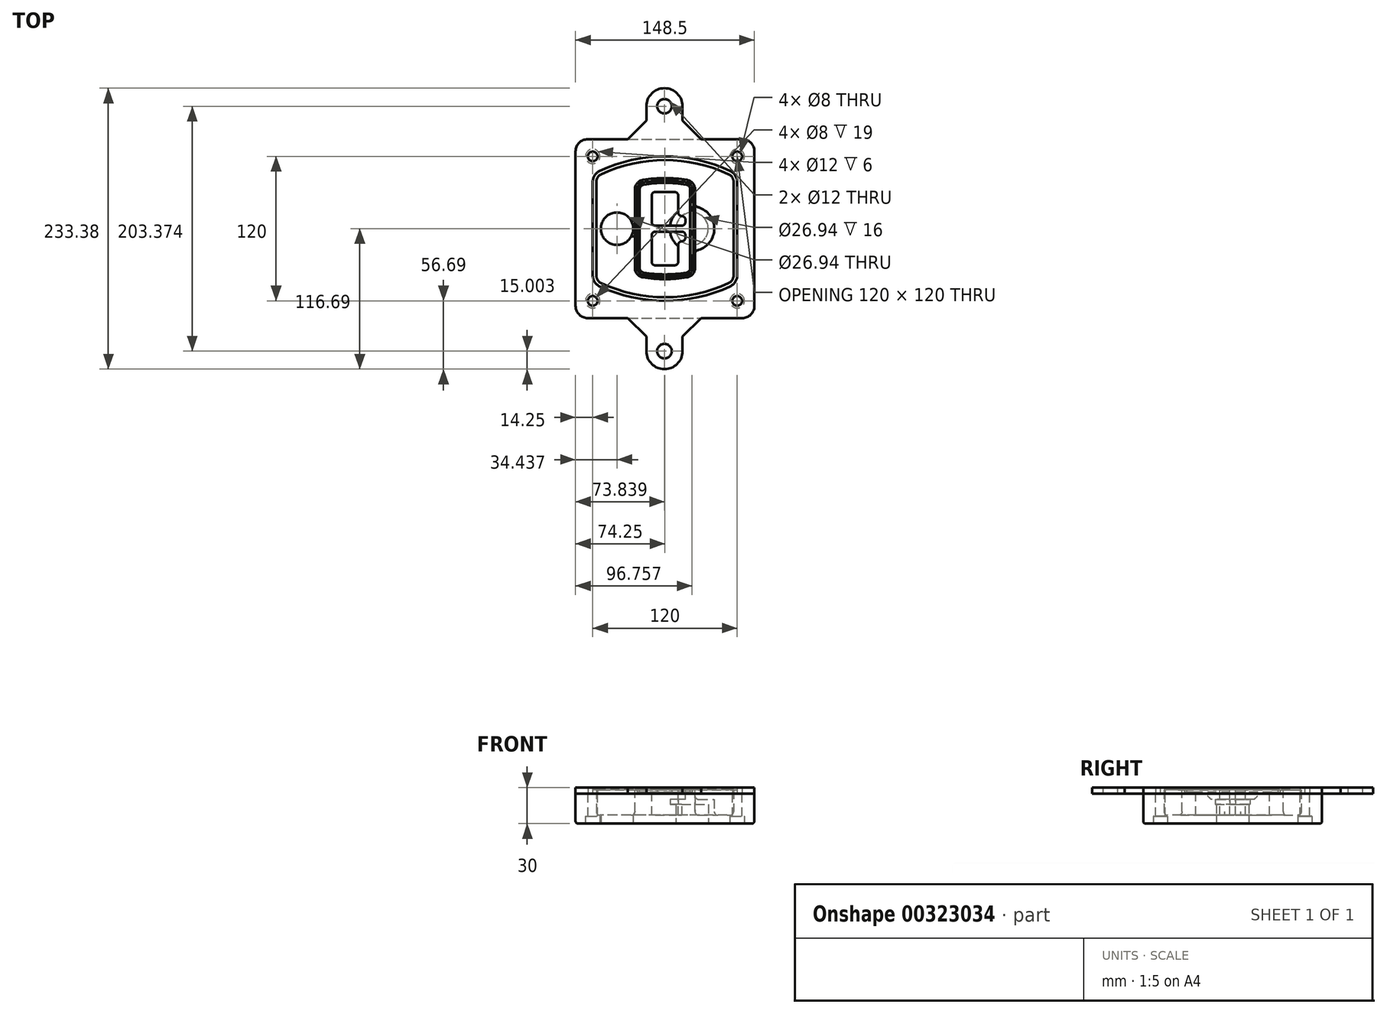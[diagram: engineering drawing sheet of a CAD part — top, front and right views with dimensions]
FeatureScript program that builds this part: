
annotation { "Feature Type Name" : "Feature", "Feature Type Description" : "" }
export const myFeature = defineFeature(function(context is Context, id is Id, definition is map)
    precondition{}
    {
        {
            var Q0;
            Q0=qCreatedBy(makeId("Top.planeOp"),FACE);
            var sketch = newSketch(context, id + "F0", { "sketchPlane" : qUnion([Q0])});
            skPoint(sketch, "E0.rect.middle", {"position": v(0, 0) * mm});
            skLineSegment(sketch, "E1.bottom", {"start": v(-64.25, -74.25) * mm, "end": v(64.25, -74.25) * mm});
            skLineSegment(sketch, "E1.top", {"start": v(-64.25, 74.25) * mm, "end": v(64.25, 74.25) * mm});
            skLineSegment(sketch, "E1.left", {"start": v(-74.25, -64.25) * mm, "end": v(-74.25, 64.25) * mm});
            skLineSegment(sketch, "E1.right", {"start": v(74.25, -64.25) * mm, "end": v(74.25, 64.25) * mm});
            skLineSegment(sketch, "E2", {"start": v(-74.25, 74.25) * mm, "end": v(74.25, -74.25) * mm, "construction": true});
            skLineSegment(sketch, "E3", {"start": v(74.25, 74.25) * mm, "end": v(-74.25, -74.25) * mm, "construction": true});
            skCircle(sketch, "E4", {"center": v(-60, 60) * mm, "radius": 4 * mm});
            skCircle(sketch, "E5", {"center": v(60, 60) * mm, "radius": 4 * mm});
            skCircle(sketch, "E6", {"center": v(60, -60) * mm, "radius": 4 * mm});
            skCircle(sketch, "E7", {"center": v(-60, -60) * mm, "radius": 4 * mm});
            skLineSegment(sketch, "E8", {"start": v(-60, 60) * mm, "end": v(60, 60) * mm, "construction": true});
            skLineSegment(sketch, "E9", {"start": v(60, 60) * mm, "end": v(60, -60) * mm, "construction": true});
            skLineSegment(sketch, "E10", {"start": v(60, -60) * mm, "end": v(-60, -60) * mm, "construction": true});
            skLineSegment(sketch, "E11", {"start": v(-60, -60) * mm, "end": v(-60, 60) * mm, "construction": true});
            skLineSegment(sketch, "E12", {"start": v(-60, 38.83) * mm, "end": v(-60, -38.83) * mm});
            skLineSegment(sketch, "E13", {"start": v(60, 38.83) * mm, "end": v(60, -38.83) * mm});
            skArc(sketch, "E14", {"start": v(54.26, 47.88) * mm, "mid": v(0, 60) * mm, "end": v(-54.26, 47.88) * mm});
            skArc(sketch, "E15", {"start": v(-54.26, -47.88) * mm, "mid": v(0, -60) * mm, "end": v(54.26, -47.88) * mm});
            skLineSegment(sketch, "E16", {"start": v(-60, 0) * mm, "end": v(60, 0) * mm, "construction": true});
            skPoint(sketch, "E17.visualSharp", {"position": v(-60, -45) * mm});
            skArc(sketch, "E17.filletArc", {"start": v(-60, -38.83) * mm, "mid": v(-58.44, -44.2) * mm, "end": v(-54.26, -47.88) * mm});
            skPoint(sketch, "E18.visualSharp", {"position": v(-60, 45) * mm});
            skArc(sketch, "E18.filletArc", {"start": v(-54.26, 47.88) * mm, "mid": v(-58.44, 44.2) * mm, "end": v(-60, 38.83) * mm});
            skPoint(sketch, "E19.visualSharp", {"position": v(60, 45) * mm});
            skArc(sketch, "E19.filletArc", {"start": v(60, 38.83) * mm, "mid": v(58.44, 44.2) * mm, "end": v(54.26, 47.88) * mm});
            skPoint(sketch, "E20.visualSharp", {"position": v(60, -45) * mm});
            skArc(sketch, "E20.filletArc", {"start": v(54.26, -47.88) * mm, "mid": v(58.44, -44.2) * mm, "end": v(60, -38.83) * mm});
            skPoint(sketch, "E21.visualSharp", {"position": v(-74.25, 74.25) * mm});
            skArc(sketch, "E21.filletArc", {"start": v(-64.25, 74.25) * mm, "mid": v(-71.32, 71.32) * mm, "end": v(-74.25, 64.25) * mm});
            skPoint(sketch, "E22.visualSharp", {"position": v(74.25, 74.25) * mm});
            skArc(sketch, "E22.filletArc", {"start": v(74.25, 64.25) * mm, "mid": v(71.32, 71.32) * mm, "end": v(64.25, 74.25) * mm});
            skPoint(sketch, "E23.visualSharp", {"position": v(74.25, -74.25) * mm});
            skArc(sketch, "E23.filletArc", {"start": v(64.25, -74.25) * mm, "mid": v(71.32, -71.32) * mm, "end": v(74.25, -64.25) * mm});
            skPoint(sketch, "E24.visualSharp", {"position": v(-74.25, -74.25) * mm});
            skArc(sketch, "E24.filletArc", {"start": v(-74.25, -64.25) * mm, "mid": v(-71.32, -71.32) * mm, "end": v(-64.25, -74.25) * mm});
            skArc(sketch, "E25.0", {"start": v(57, 38.83) * mm, "mid": v(55.9, 42.58) * mm, "end": v(52.98, 45.17) * mm});
            skLineSegment(sketch, "E25.1", {"start": v(57, 38.83) * mm, "end": v(57, -38.83) * mm});
            skArc(sketch, "E25.2", {"start": v(52.98, -45.17) * mm, "mid": v(55.9, -42.58) * mm, "end": v(57, -38.83) * mm});
            skArc(sketch, "E25.3", {"start": v(-52.98, -45.17) * mm, "mid": v(0, -57) * mm, "end": v(52.98, -45.17) * mm});
            skArc(sketch, "E25.4", {"start": v(-57, -38.83) * mm, "mid": v(-55.9, -42.58) * mm, "end": v(-52.98, -45.17) * mm});
            skArc(sketch, "E25.5", {"start": v(52.98, 45.17) * mm, "mid": v(0, 57) * mm, "end": v(-52.98, 45.17) * mm});
            skLineSegment(sketch, "E25.6", {"start": v(-57, 38.83) * mm, "end": v(-57, -38.83) * mm});
            skArc(sketch, "E25.7", {"start": v(-52.98, 45.17) * mm, "mid": v(-55.9, 42.58) * mm, "end": v(-57, 38.83) * mm});
            skArc(sketch, "E26.0", {"start": v(-55.96, 51.5) * mm, "mid": v(-61.82, 46.33) * mm, "end": v(-64, 38.83) * mm});
            skArc(sketch, "E26.1", {"start": v(55.96, 51.5) * mm, "mid": v(0, 64) * mm, "end": v(-55.96, 51.5) * mm});
            skArc(sketch, "E26.2", {"start": v(64, 38.83) * mm, "mid": v(61.82, 46.33) * mm, "end": v(55.96, 51.5) * mm});
            skLineSegment(sketch, "E26.3", {"start": v(64, 38.83) * mm, "end": v(64, -38.83) * mm});
            skArc(sketch, "E26.4", {"start": v(55.96, -51.5) * mm, "mid": v(61.82, -46.33) * mm, "end": v(64, -38.83) * mm});
            skLineSegment(sketch, "E26.5", {"start": v(-64, 38.83) * mm, "end": v(-64, -38.83) * mm});
            skArc(sketch, "E26.6", {"start": v(-55.96, -51.5) * mm, "mid": v(0, -64) * mm, "end": v(55.96, -51.5) * mm});
            skArc(sketch, "E26.7", {"start": v(-64, -38.83) * mm, "mid": v(-61.82, -46.33) * mm, "end": v(-55.96, -51.5) * mm});
            skSolve(sketch);
        }
        {
            var Q0;
            Q0=makeQuery(id+"F0.imprint","IMPRINT",FACE,{"disambiguationData":[TD([[makeQuery(id+"F0.imprint","IMPRINT",EDGE,{"derivedFrom":sQuery(id+"F0.wireOp",EDGE,"E1.bottom")}),1.0]])]});
            var Q1;
            Q1=makeQuery(id+"F0.imprint","IMPRINT",FACE,{"disambiguationData":[TD([[makeQuery(id+"F0.imprint","IMPRINT",EDGE,{"derivedFrom":sQuery(id+"F0.wireOp",EDGE,"E12")}),1.0]])]});
            var Q2;
            Q2=makeQuery(id+"F0.imprint","IMPRINT",FACE,{"disambiguationData":[TD([[makeQuery(id+"F0.imprint","IMPRINT",EDGE,{"derivedFrom":sQuery(id+"F0.wireOp",EDGE,"E25.0")}),1.0]])]});
            var Q3;
            Q3=makeQuery(id+"F0.imprint","IMPRINT",FACE,{"disambiguationData":[TD([[makeQuery(id+"F0.imprint","IMPRINT",EDGE,{"derivedFrom":sQuery(id+"F0.wireOp",EDGE,"E12")}),-1.0]])]});
            extrude(context, id + "F1", {"entities" : qUnion([Q0, Q1, Q2, Q3]), "oppositeDirection" : true, "depth" : 25 * mm});
        }
        {
            var Q0;
            Q0=makeQuery(id+"F0.imprint","IMPRINT",FACE,{"disambiguationData":[TD([[makeQuery(id+"F0.imprint","IMPRINT",EDGE,{"derivedFrom":sQuery(id+"F0.wireOp",EDGE,"E12")}),1.0]])]});
            extrude(context, id + "F2", {"entities" : qUnion([Q0]), "operationType" : NewBodyOperationType.ADD, "depth" : 3 * mm});
        }
        {
            var Q0;
            Q0=makeQuery(id+"F0.imprint","IMPRINT",FACE,{"disambiguationData":[TD([[makeQuery(id+"F0.imprint","IMPRINT",EDGE,{"derivedFrom":sQuery(id+"F0.wireOp",EDGE,"E25.0")}),1.0]])]});
            extrude(context, id + "F3", {"entities" : qUnion([Q0]), "operationType" : NewBodyOperationType.REMOVE, "oppositeDirection" : true, "depth" : 18 * mm});
        }
        {
            var Q0;
            Q0=makeQuery(id+"F2.opExtrude","CAP_FACE",FACE,{"disambiguationData":[OSD([sQuery(id+"F0.wireOp",EDGE,"E12"),sQuery(id+"F0.wireOp",EDGE,"E13"),sQuery(id+"F0.wireOp",EDGE,"E14"),sQuery(id+"F0.wireOp",EDGE,"E15"),sQuery(id+"F0.wireOp",EDGE,"E17.filletArc"),sQuery(id+"F0.wireOp",EDGE,"E18.filletArc"),sQuery(id+"F0.wireOp",EDGE,"E19.filletArc"),sQuery(id+"F0.wireOp",EDGE,"E20.filletArc"),sQuery(id+"F0.wireOp",EDGE,"E25.0"),sQuery(id+"F0.wireOp",EDGE,"E25.1"),sQuery(id+"F0.wireOp",EDGE,"E25.2"),sQuery(id+"F0.wireOp",EDGE,"E25.3"),sQuery(id+"F0.wireOp",EDGE,"E25.4"),sQuery(id+"F0.wireOp",EDGE,"E25.5"),sQuery(id+"F0.wireOp",EDGE,"E25.6"),sQuery(id+"F0.wireOp",EDGE,"E25.7")])],"isStart":false});
            var sketch = newSketch(context, id + "F4", { "sketchPlane" : qUnion([Q0])});
            skArc(sketch, "E27.0", {"start": v(-18.34, -40.45) * mm, "mid": v(0, -42) * mm, "end": v(18.34, -40.45) * mm});
            skArc(sketch, "E28.0", {"start": v(18.34, 40.45) * mm, "mid": v(0, 42) * mm, "end": v(-18.34, 40.45) * mm});
            skLineSegment(sketch, "E29", {"start": v(-25, 32.57) * mm, "end": v(-25, -32.57) * mm});
            skLineSegment(sketch, "E30", {"start": v(25, 32.57) * mm, "end": v(25, -32.57) * mm});
            skLineSegment(sketch, "E31", {"start": v(-25, 39.1) * mm, "end": v(25, 39.1) * mm, "construction": true});
            skLineSegment(sketch, "E32", {"start": v(-25, -39.1) * mm, "end": v(25, -39.1) * mm, "construction": true});
            skPoint(sketch, "E33.visualSharp", {"position": v(-25, 39.1) * mm});
            skArc(sketch, "E33.filletArc", {"start": v(-18.34, 40.45) * mm, "mid": v(-23.11, 37.73) * mm, "end": v(-25, 32.57) * mm});
            skPoint(sketch, "E34.visualSharp", {"position": v(25, 39.1) * mm});
            skArc(sketch, "E34.filletArc", {"start": v(25, 32.57) * mm, "mid": v(23.11, 37.73) * mm, "end": v(18.34, 40.45) * mm});
            skPoint(sketch, "E35.visualSharp", {"position": v(25, -39.1) * mm});
            skArc(sketch, "E35.filletArc", {"start": v(18.34, -40.45) * mm, "mid": v(23.11, -37.73) * mm, "end": v(25, -32.57) * mm});
            skPoint(sketch, "E36.visualSharp", {"position": v(-25, -39.1) * mm});
            skArc(sketch, "E36.filletArc", {"start": v(-25, -32.57) * mm, "mid": v(-23.11, -37.73) * mm, "end": v(-18.34, -40.45) * mm});
            skArc(sketch, "E37.0", {"start": v(52.98, 45.17) * mm, "mid": v(0, 57) * mm, "end": v(-52.98, 45.17) * mm});
            skArc(sketch, "E37.1", {"start": v(-52.98, 45.17) * mm, "mid": v(-55.9, 42.58) * mm, "end": v(-57, 38.83) * mm});
            skLineSegment(sketch, "E37.2", {"start": v(-57, 38.83) * mm, "end": v(-57, -38.83) * mm});
            skArc(sketch, "E37.3", {"start": v(-57, -38.83) * mm, "mid": v(-55.9, -42.58) * mm, "end": v(-52.98, -45.17) * mm});
            skArc(sketch, "E37.4", {"start": v(-52.98, -45.17) * mm, "mid": v(0, -57) * mm, "end": v(52.98, -45.17) * mm});
            skArc(sketch, "E37.5", {"start": v(52.98, -45.17) * mm, "mid": v(55.9, -42.58) * mm, "end": v(57, -38.83) * mm});
            skLineSegment(sketch, "E37.6", {"start": v(57, 38.83) * mm, "end": v(57, -38.83) * mm});
            skArc(sketch, "E37.7", {"start": v(57, 38.83) * mm, "mid": v(55.9, 42.58) * mm, "end": v(52.98, 45.17) * mm});
            skLineSegment(sketch, "E38.0", {"start": v(23, 32.57) * mm, "end": v(23, -32.57) * mm});
            skArc(sketch, "E38.1", {"start": v(18, -38.48) * mm, "mid": v(21.58, -36.44) * mm, "end": v(23, -32.57) * mm});
            skArc(sketch, "E38.2", {"start": v(-18, -38.48) * mm, "mid": v(0, -40) * mm, "end": v(18, -38.48) * mm});
            skArc(sketch, "E38.3", {"start": v(-23, -32.57) * mm, "mid": v(-21.58, -36.44) * mm, "end": v(-18, -38.48) * mm});
            skLineSegment(sketch, "E38.4", {"start": v(-23, 32.57) * mm, "end": v(-23, -32.57) * mm});
            skArc(sketch, "E38.5", {"start": v(23, 32.57) * mm, "mid": v(21.58, 36.44) * mm, "end": v(18, 38.48) * mm});
            skArc(sketch, "E38.6", {"start": v(-18, 38.48) * mm, "mid": v(-21.58, 36.44) * mm, "end": v(-23, 32.57) * mm});
            skArc(sketch, "E38.7", {"start": v(18, 38.48) * mm, "mid": v(0, 40) * mm, "end": v(-18, 38.48) * mm});
            skArc(sketch, "E39.0", {"start": v(21, 32.57) * mm, "mid": v(20.06, 35.15) * mm, "end": v(17.67, 36.5) * mm});
            skLineSegment(sketch, "E39.1", {"start": v(21, 32.57) * mm, "end": v(21, -32.57) * mm});
            skArc(sketch, "E39.2", {"start": v(17.67, -36.5) * mm, "mid": v(20.06, -35.15) * mm, "end": v(21, -32.57) * mm});
            skArc(sketch, "E39.3", {"start": v(-17.67, -36.5) * mm, "mid": v(0, -38) * mm, "end": v(17.67, -36.5) * mm});
            skArc(sketch, "E39.4", {"start": v(-21, -32.57) * mm, "mid": v(-20.06, -35.15) * mm, "end": v(-17.67, -36.5) * mm});
            skArc(sketch, "E39.5", {"start": v(17.67, 36.5) * mm, "mid": v(0, 38) * mm, "end": v(-17.67, 36.5) * mm});
            skLineSegment(sketch, "E39.6", {"start": v(-21, 32.57) * mm, "end": v(-21, -32.57) * mm});
            skArc(sketch, "E39.7", {"start": v(-17.67, 36.5) * mm, "mid": v(-20.06, 35.15) * mm, "end": v(-21, 32.57) * mm});
            skLineSegment(sketch, "E40", {"start": v(-25, 0) * mm, "end": v(25, 0) * mm, "construction": true});
            skLineSegment(sketch, "E41", {"start": v(-11, 5.5) * mm, "end": v(-11, 27.5) * mm});
            skLineSegment(sketch, "E42", {"start": v(-8, 30.5) * mm, "end": v(8, 30.5) * mm});
            skLineSegment(sketch, "E43", {"start": v(11, 27.5) * mm, "end": v(11, 13.5) * mm});
            skLineSegment(sketch, "E44", {"start": v(14, 10.5) * mm, "end": v(14, 10.5) * mm});
            skLineSegment(sketch, "E45", {"start": v(17, 7.5) * mm, "end": v(17, 5.5) * mm});
            skLineSegment(sketch, "E46", {"start": v(14, 2.5) * mm, "end": v(-8, 2.5) * mm});
            skPoint(sketch, "E47.visualSharp", {"position": v(-11, 30.5) * mm});
            skArc(sketch, "E47.filletArc", {"start": v(-8, 30.5) * mm, "mid": v(-10.12, 29.62) * mm, "end": v(-11, 27.5) * mm});
            skPoint(sketch, "E48.visualSharp", {"position": v(11, 30.5) * mm});
            skArc(sketch, "E48.filletArc", {"start": v(11, 27.5) * mm, "mid": v(10.12, 29.62) * mm, "end": v(8, 30.5) * mm});
            skPoint(sketch, "E49.visualSharp", {"position": v(11, 10.5) * mm});
            skArc(sketch, "E49.filletArc", {"start": v(11, 13.5) * mm, "mid": v(11.88, 11.38) * mm, "end": v(14, 10.5) * mm});
            skPoint(sketch, "E50.visualSharp", {"position": v(17, 10.5) * mm});
            skArc(sketch, "E50.filletArc", {"start": v(17, 7.5) * mm, "mid": v(16.12, 9.62) * mm, "end": v(14, 10.5) * mm});
            skPoint(sketch, "E51.visualSharp", {"position": v(17, 2.5) * mm});
            skArc(sketch, "E51.filletArc", {"start": v(14, 2.5) * mm, "mid": v(16.12, 3.38) * mm, "end": v(17, 5.5) * mm});
            skPoint(sketch, "E52.visualSharp", {"position": v(-11, 2.5) * mm});
            skArc(sketch, "E52.filletArc", {"start": v(-11, 5.5) * mm, "mid": v(-10.12, 3.38) * mm, "end": v(-8, 2.5) * mm});
            skLineSegment(sketch, "E53.0.MirrorCS", {"start": v(14, -2.5) * mm, "end": v(-8, -2.5) * mm});
            skArc(sketch, "E54.0.MirrorCS", {"start": v(-11, -5.5) * mm, "mid": v(-10.12, -3.38) * mm, "end": v(-8, -2.5) * mm});
            skLineSegment(sketch, "E55.0.MirrorCS", {"start": v(-11, -5.5) * mm, "end": v(-11, -27.5) * mm});
            skArc(sketch, "E56.0.MirrorCS", {"start": v(-8, -30.5) * mm, "mid": v(-10.12, -29.62) * mm, "end": v(-11, -27.5) * mm});
            skLineSegment(sketch, "E57.0.MirrorCS", {"start": v(-8, -30.5) * mm, "end": v(8, -30.5) * mm});
            skArc(sketch, "E58.0.MirrorCS", {"start": v(11, -27.5) * mm, "mid": v(10.12, -29.62) * mm, "end": v(8, -30.5) * mm});
            skLineSegment(sketch, "E59.0.MirrorCS", {"start": v(11, -27.5) * mm, "end": v(11, -13.5) * mm});
            skArc(sketch, "E60.0.MirrorCS", {"start": v(11, -13.5) * mm, "mid": v(11.88, -11.38) * mm, "end": v(14, -10.5) * mm});
            skArc(sketch, "E61.0.MirrorCS", {"start": v(17, -7.5) * mm, "mid": v(16.12, -9.62) * mm, "end": v(14, -10.5) * mm});
            skLineSegment(sketch, "E62.0.MirrorCS", {"start": v(17, -7.5) * mm, "end": v(17, -5.5) * mm});
            skArc(sketch, "E63.0.MirrorCS", {"start": v(14, -2.5) * mm, "mid": v(16.12, -3.38) * mm, "end": v(17, -5.5) * mm});
            skSolve(sketch);
        }
        {
            var Q0;
            Q0=makeQuery(id+"F4.imprint","IMPRINT",FACE,{"disambiguationData":[TD([[makeQuery(id+"F4.imprint","IMPRINT",EDGE,{"derivedFrom":sQuery(id+"F4.wireOp",EDGE,"E27.0")}),1.0]])]});
            var Q1;
            Q1=makeQuery(id+"F4.imprint","IMPRINT",FACE,{"disambiguationData":[TD([[makeQuery(id+"F4.imprint","IMPRINT",EDGE,{"derivedFrom":sQuery(id+"F4.wireOp",EDGE,"E38.0")}),-1.0]])]});
            var Q2;
            Q2=makeQuery(id+"F4.imprint","IMPRINT",FACE,{"disambiguationData":[TD([[makeQuery(id+"F4.imprint","IMPRINT",EDGE,{"derivedFrom":sQuery(id+"F4.wireOp",EDGE,"E39.0")}),1.0]])]});
            extrude(context, id + "F5", {"entities" : qUnion([Q0, Q1, Q2]), "operationType" : NewBodyOperationType.ADD, "endBound" : BoundingType.UP_TO_NEXT, "oppositeDirection" : true, "depth" : 25 * mm});
        }
        {
            var Q0;
            Q0=makeQuery(id+"F4.imprint","IMPRINT",FACE,{"disambiguationData":[TD([[makeQuery(id+"F4.imprint","IMPRINT",EDGE,{"derivedFrom":sQuery(id+"F4.wireOp",EDGE,"E38.0")}),-1.0]])]});
            extrude(context, id + "F6", {"entities" : qUnion([Q0]), "operationType" : NewBodyOperationType.REMOVE, "oppositeDirection" : true, "depth" : 2 * mm});
        }
        {
            var Q0;
            Q0=makeQuery(id+"F1.opExtrude","CAP_FACE",FACE,{"disambiguationData":[OSD([sQuery(id+"F0.wireOp",EDGE,"E1.bottom"),sQuery(id+"F0.wireOp",EDGE,"E1.top"),sQuery(id+"F0.wireOp",EDGE,"E1.left"),sQuery(id+"F0.wireOp",EDGE,"E1.right"),sQuery(id+"F0.wireOp",EDGE,"E4"),sQuery(id+"F0.wireOp",EDGE,"E5"),sQuery(id+"F0.wireOp",EDGE,"E6"),sQuery(id+"F0.wireOp",EDGE,"E7"),sQuery(id+"F0.wireOp",EDGE,"E21.filletArc"),sQuery(id+"F0.wireOp",EDGE,"E22.filletArc"),sQuery(id+"F0.wireOp",EDGE,"E23.filletArc"),sQuery(id+"F0.wireOp",EDGE,"E24.filletArc")])],"isStart":false});
            var sketch = newSketch(context, id + "F7", { "sketchPlane" : qUnion([Q0])});
            skCircle(sketch, "E64", {"center": v(22.5, 0) * mm, "radius": 13.47 * mm});
            skCircle(sketch, "E65", {"center": v(-39.81, 0) * mm, "radius": 13.47 * mm});
            skLineSegment(sketch, "E66", {"start": v(74.25, 0) * mm, "end": v(-74.25, 0) * mm});
            skCircle(sketch, "E67", {"center": v(22.5, 0) * mm, "radius": 18.47 * mm});
            skCircle(sketch, "E68", {"center": v(60, -60) * mm, "radius": 6 * mm});
            skCircle(sketch, "E69", {"center": v(-60, -60) * mm, "radius": 6 * mm});
            skCircle(sketch, "E70", {"center": v(-60, 60) * mm, "radius": 6 * mm});
            skCircle(sketch, "E71", {"center": v(60, 60) * mm, "radius": 6 * mm});
            skSolve(sketch);
        }
        {
            var Q0;
            {var subQ1=sQuery(id+"F7.wireOp",EDGE,"E66");var subQ4=sQuery(id+"F7.wireOp",EDGE,"E64");var subQ6=makeQuery(id+"F7.imprint","INTERSECT",VERTEX,{"disambiguationData":[OD(0.0)],"derivedFrom":[subQ4,subQ1]});Q0=makeQuery(id+"F7.imprint","IMPRINT",FACE,{"disambiguationData":[TD([[makeQuery(id+"F7.imprint","IMPRINT",EDGE,{"disambiguationData":[TD([[subQ6,-1.0]])],"derivedFrom":subQ4}),-1.0]])]});}
            var Q1;
            {var subQ0=sQuery(id+"F7.wireOp",EDGE,"E66");var subQ1=sQuery(id+"F7.wireOp",EDGE,"E64");var subQ3=makeQuery(id+"F7.imprint","INTERSECT",VERTEX,{"disambiguationData":[OD(0.0)],"derivedFrom":[subQ1,subQ0]});Q1=makeQuery(id+"F7.imprint","IMPRINT",FACE,{"disambiguationData":[TD([[makeQuery(id+"F7.imprint","IMPRINT",EDGE,{"disambiguationData":[TD([[subQ3,-1.0]])],"derivedFrom":subQ1}),1.0]])]});}
            var Q2;
            {var subQ0=sQuery(id+"F7.wireOp",EDGE,"E66");var subQ1=sQuery(id+"F7.wireOp",EDGE,"E64");var subQ3=makeQuery(id+"F7.imprint","INTERSECT",VERTEX,{"disambiguationData":[OD(0.0)],"derivedFrom":[subQ1,subQ0]});Q2=makeQuery(id+"F7.imprint","IMPRINT",FACE,{"disambiguationData":[TD([[makeQuery(id+"F7.imprint","IMPRINT",EDGE,{"disambiguationData":[TD([[subQ3,1.0]])],"derivedFrom":subQ1}),1.0]])]});}
            var Q3;
            {var subQ1=sQuery(id+"F7.wireOp",EDGE,"E66");var subQ4=sQuery(id+"F7.wireOp",EDGE,"E64");var subQ6=makeQuery(id+"F7.imprint","INTERSECT",VERTEX,{"disambiguationData":[OD(0.0)],"derivedFrom":[subQ4,subQ1]});Q3=makeQuery(id+"F7.imprint","IMPRINT",FACE,{"disambiguationData":[TD([[makeQuery(id+"F7.imprint","IMPRINT",EDGE,{"disambiguationData":[TD([[subQ6,1.0]])],"derivedFrom":subQ4}),-1.0]])]});}
            extrude(context, id + "F8", {"entities" : qUnion([Q0, Q1, Q2, Q3]), "operationType" : NewBodyOperationType.ADD, "oppositeDirection" : true, "depth" : 20 * mm});
        }
        {
            var Q0;
            {var subQ0=sQuery(id+"F7.wireOp",EDGE,"E66");var subQ1=sQuery(id+"F7.wireOp",EDGE,"E64");var subQ3=makeQuery(id+"F7.imprint","INTERSECT",VERTEX,{"disambiguationData":[OD(0.0)],"derivedFrom":[subQ1,subQ0]});Q0=makeQuery(id+"F7.imprint","IMPRINT",FACE,{"disambiguationData":[TD([[makeQuery(id+"F7.imprint","IMPRINT",EDGE,{"disambiguationData":[TD([[subQ3,-1.0]])],"derivedFrom":subQ1}),1.0]])]});}
            var Q1;
            {var subQ0=sQuery(id+"F7.wireOp",EDGE,"E66");var subQ1=sQuery(id+"F7.wireOp",EDGE,"E64");var subQ3=makeQuery(id+"F7.imprint","INTERSECT",VERTEX,{"disambiguationData":[OD(0.0)],"derivedFrom":[subQ1,subQ0]});Q1=makeQuery(id+"F7.imprint","IMPRINT",FACE,{"disambiguationData":[TD([[makeQuery(id+"F7.imprint","IMPRINT",EDGE,{"disambiguationData":[TD([[subQ3,1.0]])],"derivedFrom":subQ1}),1.0]])]});}
            extrude(context, id + "F9", {"entities" : qUnion([Q0, Q1]), "operationType" : NewBodyOperationType.REMOVE, "oppositeDirection" : true, "depth" : 16 * mm});
        }
        {
            var Q0;
            {var subQ0=sQuery(id+"F7.wireOp",EDGE,"E66");var subQ1=sQuery(id+"F7.wireOp",EDGE,"E65");var subQ3=makeQuery(id+"F7.imprint","INTERSECT",VERTEX,{"disambiguationData":[OD(0.0)],"derivedFrom":[subQ1,subQ0]});Q0=makeQuery(id+"F7.imprint","IMPRINT",FACE,{"disambiguationData":[TD([[makeQuery(id+"F7.imprint","IMPRINT",EDGE,{"disambiguationData":[TD([[subQ3,-1.0]])],"derivedFrom":subQ1}),1.0]])]});}
            var Q1;
            {var subQ0=sQuery(id+"F7.wireOp",EDGE,"E66");var subQ1=sQuery(id+"F7.wireOp",EDGE,"E65");var subQ3=makeQuery(id+"F7.imprint","INTERSECT",VERTEX,{"disambiguationData":[OD(0.0)],"derivedFrom":[subQ1,subQ0]});Q1=makeQuery(id+"F7.imprint","IMPRINT",FACE,{"disambiguationData":[TD([[makeQuery(id+"F7.imprint","IMPRINT",EDGE,{"disambiguationData":[TD([[subQ3,1.0]])],"derivedFrom":subQ1}),1.0]])]});}
            extrude(context, id + "F10", {"entities" : qUnion([Q0, Q1]), "operationType" : NewBodyOperationType.REMOVE, "oppositeDirection" : true, "depth" : 25 * mm});
        }
        {
            var Q0;
            Q0=makeQuery(id+"F7.imprint","IMPRINT",FACE,{"disambiguationData":[TD([[makeQuery(id+"F7.imprint","IMPRINT",EDGE,{"derivedFrom":sQuery(id+"F7.wireOp",EDGE,"E68")}),1.0]])]});
            var Q1;
            Q1=makeQuery(id+"F7.imprint","IMPRINT",FACE,{"disambiguationData":[TD([[makeQuery(id+"F7.imprint","IMPRINT",EDGE,{"derivedFrom":makeQuery(id+"F1.opExtrude","CAP_EDGE",EDGE,{"disambiguationData":[OSD([sQuery(id+"F0.wireOp",EDGE,"E5")])],"isStart":false})}),-1.0]])]});
            var Q2;
            Q2=makeQuery(id+"F7.imprint","IMPRINT",FACE,{"disambiguationData":[TD([[makeQuery(id+"F7.imprint","IMPRINT",EDGE,{"derivedFrom":sQuery(id+"F7.wireOp",EDGE,"E69")}),1.0]])]});
            var Q3;
            Q3=makeQuery(id+"F7.imprint","IMPRINT",FACE,{"disambiguationData":[TD([[makeQuery(id+"F7.imprint","IMPRINT",EDGE,{"derivedFrom":makeQuery(id+"F1.opExtrude","CAP_EDGE",EDGE,{"disambiguationData":[OSD([sQuery(id+"F0.wireOp",EDGE,"E4")])],"isStart":false})}),-1.0]])]});
            var Q4;
            Q4=makeQuery(id+"F7.imprint","IMPRINT",FACE,{"disambiguationData":[TD([[makeQuery(id+"F7.imprint","IMPRINT",EDGE,{"derivedFrom":sQuery(id+"F7.wireOp",EDGE,"E70")}),1.0]])]});
            var Q5;
            Q5=makeQuery(id+"F7.imprint","IMPRINT",FACE,{"disambiguationData":[TD([[makeQuery(id+"F7.imprint","IMPRINT",EDGE,{"derivedFrom":makeQuery(id+"F1.opExtrude","CAP_EDGE",EDGE,{"disambiguationData":[OSD([sQuery(id+"F0.wireOp",EDGE,"E7")])],"isStart":false})}),-1.0]])]});
            var Q6;
            Q6=makeQuery(id+"F7.imprint","IMPRINT",FACE,{"disambiguationData":[TD([[makeQuery(id+"F7.imprint","IMPRINT",EDGE,{"derivedFrom":sQuery(id+"F7.wireOp",EDGE,"E71")}),1.0]])]});
            var Q7;
            Q7=makeQuery(id+"F7.imprint","IMPRINT",FACE,{"disambiguationData":[TD([[makeQuery(id+"F7.imprint","IMPRINT",EDGE,{"derivedFrom":makeQuery(id+"F1.opExtrude","CAP_EDGE",EDGE,{"disambiguationData":[OSD([sQuery(id+"F0.wireOp",EDGE,"E6")])],"isStart":false})}),-1.0]])]});
            extrude(context, id + "F11", {"entities" : qUnion([Q0, Q1, Q2, Q3, Q4, Q5, Q6, Q7]), "operationType" : NewBodyOperationType.REMOVE, "oppositeDirection" : true, "depth" : 6 * mm});
        }
        {
            var Q0;
            Q0=makeQuery(id+"F9.boolean.opBoolean","COPY",FACE,{"derivedFrom":makeQuery(id+"F9.opExtrude","CAP_FACE",FACE,{"disambiguationData":[OSD([sQuery(id+"F7.wireOp",EDGE,"E64")])],"isStart":false})});
            var sketch = newSketch(context, id + "F12", { "sketchPlane" : qUnion([Q0])});
            skArc(sketch, "E72.0", {"start": v(11, 14.45) * mm, "mid": v(6.45, 9.13) * mm, "end": v(4.2, 2.5) * mm});
            skArc(sketch, "E72.1", {"start": v(4.2, -2.5) * mm, "mid": v(6.45, -9.13) * mm, "end": v(11, -14.45) * mm});
            skLineSegment(sketch, "E73", {"start": v(4.2, -2.5) * mm, "end": v(14, -2.5) * mm});
            skLineSegment(sketch, "E74.0", {"start": v(14, 2.5) * mm, "end": v(4.2, 2.5) * mm});
            skArc(sketch, "E74.1", {"start": v(14, 2.5) * mm, "mid": v(16.12, 3.38) * mm, "end": v(17, 5.5) * mm});
            skLineSegment(sketch, "E74.2", {"start": v(17, 7.5) * mm, "end": v(17, 5.5) * mm});
            skArc(sketch, "E74.3", {"start": v(17, 7.5) * mm, "mid": v(16.12, 9.62) * mm, "end": v(14, 10.5) * mm});
            skArc(sketch, "E74.4", {"start": v(11, 13.5) * mm, "mid": v(11.88, 11.38) * mm, "end": v(14, 10.5) * mm});
            skLineSegment(sketch, "E74.5", {"start": v(11, 14.45) * mm, "end": v(11, 13.5) * mm});
            skLineSegment(sketch, "E74.7", {"start": v(14, -2.5) * mm, "end": v(4.2, -2.5) * mm});
            skArc(sketch, "E74.8", {"start": v(14, -2.5) * mm, "mid": v(16.12, -3.38) * mm, "end": v(17, -5.5) * mm});
            skLineSegment(sketch, "E74.9", {"start": v(17, -7.5) * mm, "end": v(17, -5.5) * mm});
            skArc(sketch, "E74.10", {"start": v(17, -7.5) * mm, "mid": v(16.12, -9.62) * mm, "end": v(14, -10.5) * mm});
            skArc(sketch, "E74.11", {"start": v(11, -13.5) * mm, "mid": v(11.88, -11.38) * mm, "end": v(14, -10.5) * mm});
            skLineSegment(sketch, "E74.12", {"start": v(11, -14.45) * mm, "end": v(11, -13.5) * mm});
            skPoint(sketch, "E75.orphan", {"position": v(11, -27.5) * mm});
            skPoint(sketch, "E76.orphan", {"position": v(-8, -2.5) * mm});
            skPoint(sketch, "E77.orphan", {"position": v(-8, 2.5) * mm});
            skPoint(sketch, "E78.orphan", {"position": v(11, 27.5) * mm});
            skSolve(sketch);
        }
        {
            var Q0;
            {var subQ7=sQuery(id+"F12.wireOp",EDGE,"E72.0");var subQ14=sQuery(id+"F12.wireOp",EDGE,"E72.1");var subQ16=sQuery(id+"F12.wireOp",EDGE,"E74.1");var subQ18=sQuery(id+"F12.wireOp",EDGE,"E74.8");Q0=qUnion([makeQuery(id+"F12.imprint","IMPRINT",FACE,{"disambiguationData":[TD([[makeQuery(id+"F12.imprint","IMPRINT",EDGE,{"derivedFrom":subQ7}),1.0]])]}),makeQuery(id+"F12.imprint","IMPRINT",FACE,{"disambiguationData":[TD([[makeQuery(id+"F12.imprint","IMPRINT",EDGE,{"derivedFrom":subQ14}),1.0]])]}),makeQuery(id+"F12.imprint","IMPRINT",FACE,{"disambiguationData":[TD([[makeQuery(id+"F12.imprint","IMPRINT",EDGE,{"derivedFrom":subQ16}),1.0]])]}),makeQuery(id+"F12.imprint","IMPRINT",FACE,{"disambiguationData":[TD([[makeQuery(id+"F12.imprint","IMPRINT",EDGE,{"derivedFrom":subQ18}),-1.0]])]})]);}
            var Q1;
            Q1=makeQuery(id+"F5.boolean.opBoolean","SPLIT",FACE,{"disambiguationData":[TD([makeQuery(id+"F5.opExtrude","SWEPT_FACE",FACE,{"disambiguationData":[OSD([sQuery(id+"F4.wireOp",EDGE,"E41")])]})])],"derivedFrom":makeQuery(id+"F3.boolean.opBoolean","COPY",FACE,{"derivedFrom":makeQuery(id+"F3.opExtrude","CAP_FACE",FACE,{"disambiguationData":[OSD([sQuery(id+"F0.wireOp",EDGE,"E25.0"),sQuery(id+"F0.wireOp",EDGE,"E25.1"),sQuery(id+"F0.wireOp",EDGE,"E25.2"),sQuery(id+"F0.wireOp",EDGE,"E25.3"),sQuery(id+"F0.wireOp",EDGE,"E25.4"),sQuery(id+"F0.wireOp",EDGE,"E25.5"),sQuery(id+"F0.wireOp",EDGE,"E25.6"),sQuery(id+"F0.wireOp",EDGE,"E25.7")])],"isStart":false})})});
            extrude(context, id + "F13", {"entities" : qUnion([Q0]), "operationType" : NewBodyOperationType.REMOVE, "endBound" : BoundingType.UP_TO_SURFACE, "endBoundEntityFace" : qUnion([Q1]), "depth" : 25 * mm});
        }
        {
            var Q0;
            Q0=makeQuery(id+"F3.boolean.opBoolean","COPY",EDGE,{"derivedFrom":makeQuery(id+"F3.opExtrude","CAP_EDGE",EDGE,{"disambiguationData":[OSD([sQuery(id+"F0.wireOp",EDGE,"E25.6")])],"isStart":false})});
            var Q1;
            Q1=makeQuery(id+"F8.boolean.opBoolean","INTERSECT",EDGE,{"derivedFrom":[makeQuery(id+"F5.opExtrude","SWEPT_FACE",FACE,{"disambiguationData":[OSD([sQuery(id+"F4.wireOp",EDGE,"E30")])]}),makeQuery(id+"F8.opExtrude","CAP_FACE",FACE,{"disambiguationData":[OSD([sQuery(id+"F7.wireOp",EDGE,"E67")])],"isStart":false})]});
            var Q2;
            Q2=makeQuery(id+"F8.boolean.opBoolean","INTERSECT",EDGE,{"disambiguationData":[OD(1.0)],"derivedFrom":[makeQuery(id+"F5.opExtrude","SWEPT_FACE",FACE,{"disambiguationData":[OSD([sQuery(id+"F4.wireOp",EDGE,"E30")])]}),makeQuery(id+"F8.opExtrude","SWEPT_FACE",FACE,{"disambiguationData":[OSD([sQuery(id+"F7.wireOp",EDGE,"E67")])]})]});
            var Q3;
            {var subQ0=sQuery(id+"F4.wireOp",EDGE,"E30");Q3=makeQuery(id+"F8.boolean.opBoolean","SPLIT",EDGE,{"disambiguationData":[TD([makeQuery(id+"F5.opExtrude","SWEPT_FACE",FACE,{"disambiguationData":[OSD([sQuery(id+"F4.wireOp",EDGE,"E35.filletArc")])]})])],"derivedFrom":makeQuery(id+"F5.opExtrude","CAP_EDGE",EDGE,{"disambiguationData":[OSD([subQ0])],"isStart":false})});}
            var Q4;
            {var subQ0=sQuery(id+"F0.wireOp",EDGE,"E25.7");var subQ1=sQuery(id+"F0.wireOp",EDGE,"E25.1");var subQ2=sQuery(id+"F0.wireOp",EDGE,"E25.6");var subQ3=sQuery(id+"F0.wireOp",EDGE,"E25.5");var subQ4=sQuery(id+"F0.wireOp",EDGE,"E25.4");var subQ5=sQuery(id+"F0.wireOp",EDGE,"E25.0");var subQ6=sQuery(id+"F0.wireOp",EDGE,"E25.2");var subQ7=sQuery(id+"F0.wireOp",EDGE,"E25.3");Q4=makeQuery(id+"F8.boolean.opBoolean","INTERSECT",EDGE,{"derivedFrom":[makeQuery(id+"F5.boolean.opBoolean","SPLIT",FACE,{"disambiguationData":[TD([makeQuery(id+"F2.opExtrude","SWEPT_FACE",FACE,{"disambiguationData":[OSD([subQ5])]})])],"derivedFrom":makeQuery(id+"F3.boolean.opBoolean","COPY",FACE,{"derivedFrom":makeQuery(id+"F3.opExtrude","CAP_FACE",FACE,{"disambiguationData":[OSD([subQ5,subQ1,subQ6,subQ7,subQ4,subQ3,subQ2,subQ0])],"isStart":false})})}),makeQuery(id+"F8.opExtrude","SWEPT_FACE",FACE,{"disambiguationData":[OSD([sQuery(id+"F7.wireOp",EDGE,"E67")])]})]});}
            var Q5;
            Q5=makeQuery(id+"F8.boolean.opBoolean","INTERSECT",EDGE,{"disambiguationData":[OD(0.0)],"derivedFrom":[makeQuery(id+"F5.opExtrude","SWEPT_FACE",FACE,{"disambiguationData":[OSD([sQuery(id+"F4.wireOp",EDGE,"E30")])]}),makeQuery(id+"F8.opExtrude","SWEPT_FACE",FACE,{"disambiguationData":[OSD([sQuery(id+"F7.wireOp",EDGE,"E67")])]})]});
            fillet(context, id + "F14", {"entities" : qUnion([Q0, Q1, Q2, Q3, Q4, Q5]), "radius" : 3 * mm, "tangentPropagation" : true, "allowEdgeOverflow" : false});
        }
        {
            var Q0;
            Q0=makeQuery(id+"F1.opExtrude","CAP_EDGE",EDGE,{"disambiguationData":[OSD([sQuery(id+"F0.wireOp",EDGE,"E1.bottom")])],"isStart":false});
            fillet(context, id + "F15", {"entities" : qUnion([Q0]), "radius" : 2 * mm, "tangentPropagation" : true, "allowEdgeOverflow" : false});
        }
        {
            var Q0;
            {var subQ0=sQuery(id+"F0.wireOp",EDGE,"E21.filletArc");var subQ1=sQuery(id+"F0.wireOp",EDGE,"E7");var subQ2=sQuery(id+"F0.wireOp",EDGE,"E6");var subQ3=sQuery(id+"F0.wireOp",EDGE,"E5");var subQ4=sQuery(id+"F0.wireOp",EDGE,"E4");var subQ5=sQuery(id+"F0.wireOp",EDGE,"E22.filletArc");var subQ6=sQuery(id+"F0.wireOp",EDGE,"E1.bottom");var subQ7=sQuery(id+"F0.wireOp",EDGE,"E1.right");var subQ8=sQuery(id+"F0.wireOp",EDGE,"E1.top");var subQ9=sQuery(id+"F0.wireOp",EDGE,"E1.left");var subQ10=sQuery(id+"F0.wireOp",EDGE,"E23.filletArc");var subQ11=sQuery(id+"F0.wireOp",EDGE,"E24.filletArc");Q0=makeQuery(id+"F2.boolean.opBoolean","SPLIT",FACE,{"disambiguationData":[TD([makeQuery(id+"F1.opExtrude","SWEPT_FACE",FACE,{"disambiguationData":[OSD([subQ6])]})])],"derivedFrom":makeQuery(id+"F1.opExtrude","CAP_FACE",FACE,{"disambiguationData":[OSD([subQ6,subQ8,subQ9,subQ7,subQ4,subQ3,subQ2,subQ1,subQ0,subQ5,subQ10,subQ11])],"isStart":true})});}
            var sketch = newSketch(context, id + "F16", { "sketchPlane" : qUnion([Q0])});
            skLineSegment(sketch, "E79", {"start": v(-15.41, 89.69) * mm, "end": v(-15.41, 101.69) * mm});
            skArc(sketch, "E80", {"start": v(14.59, 101.69) * mm, "mid": v(-0.41, 116.69) * mm, "end": v(-15.41, 101.69) * mm});
            skCircle(sketch, "E81", {"center": v(-0.41, 101.69) * mm, "radius": 6 * mm});
            skLineSegment(sketch, "E82", {"start": v(118.1, 0) * mm, "end": v(-115.76, 0) * mm});
            skPoint(sketch, "E82.endSnap0", {"position": v(60, 0) * mm});
            skLineSegment(sketch, "E83", {"start": v(14.59, 101.69) * mm, "end": v(14.59, 89.69) * mm});
            skLineSegment(sketch, "E84", {"start": v(14.59, 89.69) * mm, "end": v(30.03, 74.25) * mm});
            skLineSegment(sketch, "E85", {"start": v(-15.41, 89.69) * mm, "end": v(-30.85, 74.25) * mm});
            skLineSegment(sketch, "E86.MirrorCS", {"start": v(14.59, -89.69) * mm, "end": v(30.03, -74.25) * mm});
            skLineSegment(sketch, "E87.MirrorCS", {"start": v(14.59, -101.69) * mm, "end": v(14.59, -89.69) * mm});
            skArc(sketch, "E88.MirrorCS", {"start": v(14.59, -101.69) * mm, "mid": v(-0.41, -116.69) * mm, "end": v(-15.41, -101.69) * mm});
            skLineSegment(sketch, "E89.MirrorCS", {"start": v(-15.41, -89.69) * mm, "end": v(-15.41, -101.69) * mm});
            skLineSegment(sketch, "E90.MirrorCS", {"start": v(-15.41, -89.69) * mm, "end": v(-30.85, -74.25) * mm});
            skCircle(sketch, "E91.MirrorC", {"center": v(-0.41, -101.69) * mm, "radius": 6 * mm});
            skSolve(sketch);
        }
        {
            var Q0;
            {var subQ1=sQuery(id+"F16.wireOp",EDGE,"3yVoNcxS-1F8g-ADg9-q7Y3-fsagkn9f3hTi");Q0=makeQuery(id+"F16.imprint","IMPRINT",FACE,{"disambiguationData":[TD([[makeQuery(id+"F16.imprint","IMPRINT",EDGE,{"derivedFrom":subQ1}),-1.0]])]});}
            var Q1;
            {var subQ0=sQuery(id+"F16.wireOp",EDGE,"6124975b-90e3-42c7-8484-f201a9f1b6830.MirrorCS");Q1=makeQuery(id+"F16.imprint","IMPRINT",FACE,{"disambiguationData":[TD([[makeQuery(id+"F16.imprint","IMPRINT",EDGE,{"derivedFrom":subQ0}),1.0]])]});}
            var Q2;
            Q2=makeQuery(id+"F16.imprint","IMPRINT",FACE,{"disambiguationData":[TD([[makeQuery(id+"F16.imprint","IMPRINT",EDGE,{"derivedFrom":makeQuery(id+"F1.opExtrude","CAP_EDGE",EDGE,{"disambiguationData":[OSD([sQuery(id+"F0.wireOp",EDGE,"E4")])],"isStart":true})}),-1.0]])]});
            var Q3;
            Q3=makeQuery(id+"F16.imprint","IMPRINT",FACE,{"disambiguationData":[TD([[makeQuery(id+"F16.imprint","IMPRINT",EDGE,{"derivedFrom":makeQuery(id+"F1.opExtrude","CAP_EDGE",EDGE,{"disambiguationData":[OSD([sQuery(id+"F0.wireOp",EDGE,"E6")])],"isStart":true})}),-1.0]])]});
            var Q4;
            {var subQ0=sQuery(id+"F16.wireOp",EDGE,"cc54fde0-1057-406a-b5e8-0b41f291de9c0.MirrorCS");Q4=makeQuery(id+"F16.imprint","IMPRINT",FACE,{"disambiguationData":[TD([[makeQuery(id+"F16.imprint","IMPRINT",EDGE,{"derivedFrom":subQ0}),1.0]])]});}
            var Q5;
            Q5=makeQuery(id+"F16.imprint","IMPRINT",FACE,{"disambiguationData":[TD([[makeQuery(id+"F16.imprint","IMPRINT",EDGE,{"derivedFrom":sQuery(id+"F16.wireOp",EDGE,"E79")}),-1.0]])]});
            var Q6;
            {var subQ0=sQuery(id+"F16.wireOp",EDGE,"E86.MirrorCS");Q6=makeQuery(id+"F16.imprint","IMPRINT",FACE,{"disambiguationData":[TD([[makeQuery(id+"F16.imprint","IMPRINT",EDGE,{"derivedFrom":subQ0}),1.0]])]});}
            extrude(context, id + "F17", {"entities" : qUnion([Q0, Q1, Q2, Q3, Q4, Q5, Q6]), "depth" : 5 * mm});
        }
    });
